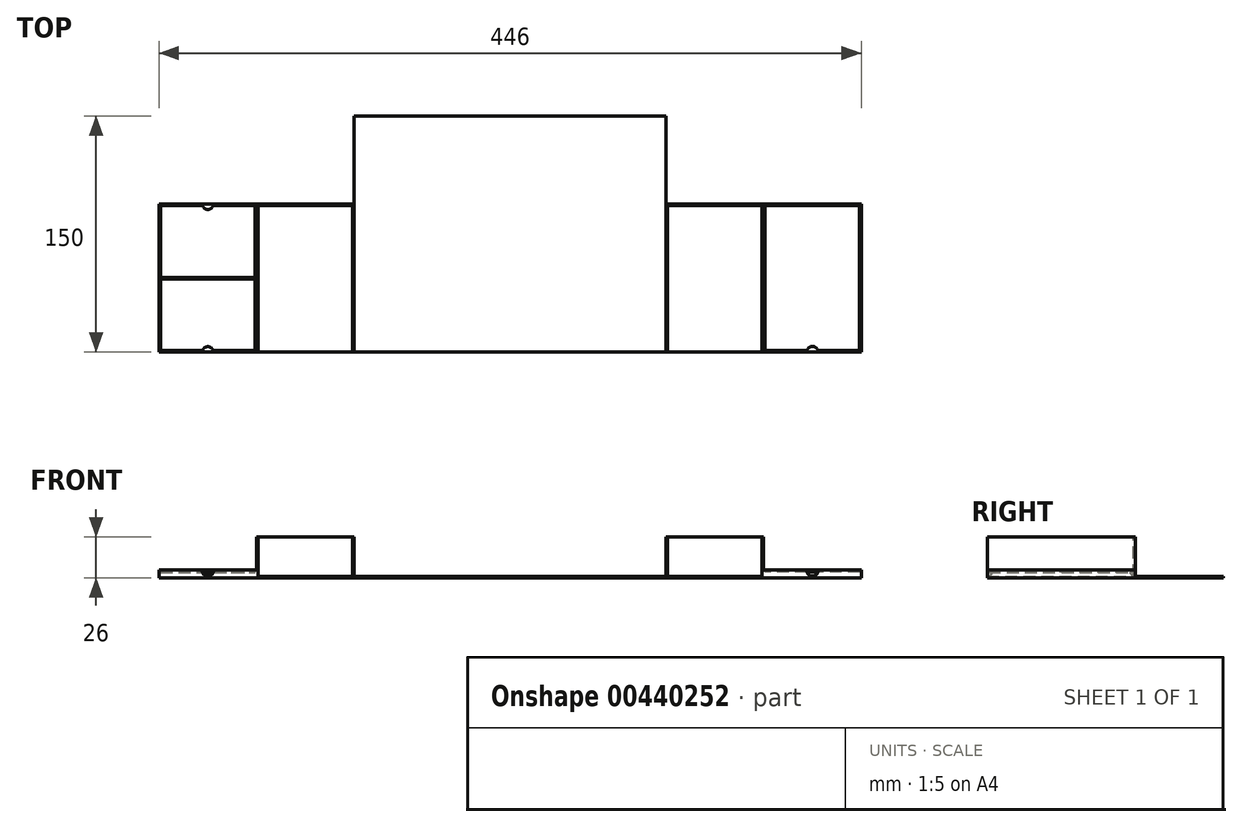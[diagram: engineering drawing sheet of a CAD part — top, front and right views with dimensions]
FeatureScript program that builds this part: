
annotation { "Feature Type Name" : "Feature", "Feature Type Description" : "" }
export const myFeature = defineFeature(function(context is Context, id is Id, definition is map)
    precondition{}
    {
        {
            var Q0;
            Q0=qCreatedBy(makeId("Top.planeOp"),FACE);
            var sketch = newSketch(context, id + "F0", { "sketchPlane" : qUnion([Q0])});
            skLineSegment(sketch, "E0", {"start": v(0, 0) * mm, "end": v(322, 0) * mm});
            skLineSegment(sketch, "E1", {"start": v(322, 0) * mm, "end": v(322, 94) * mm});
            skLineSegment(sketch, "E2", {"start": v(322, 94) * mm, "end": v(261, 94) * mm});
            skLineSegment(sketch, "E3", {"start": v(261, 94) * mm, "end": v(261, 150) * mm});
            skLineSegment(sketch, "E4", {"start": v(261, 150) * mm, "end": v(61, 150) * mm});
            skLineSegment(sketch, "E5", {"start": v(61, 150) * mm, "end": v(61, 94) * mm});
            skLineSegment(sketch, "E6", {"start": v(61, 94) * mm, "end": v(0, 94) * mm});
            skLineSegment(sketch, "E7", {"start": v(0, 94) * mm, "end": v(0, 0) * mm});
            skSolve(sketch);
        }
        {
            var Q0;
            Q0=makeQuery(id+"F0.imprint","IMPRINT",FACE,{"disambiguationData":[TD([[makeQuery(id+"F0.imprint","IMPRINT",EDGE,{"derivedFrom":sQuery(id+"F0.wireOp",EDGE,"E0")}),1.0]])]});
            extrude(context, id + "F1", {"entities" : qUnion([Q0]), "depth" : 26 * mm});
        }
        {
            var Q0;
            Q0=makeQuery(id+"F1.opExtrude","SWEPT_FACE",FACE,{"disambiguationData":[OSD([sQuery(id+"F0.wireOp",EDGE,"E7")])]});
            var sketch = newSketch(context, id + "F2", { "sketchPlane" : qUnion([Q0])});
            skLineSegment(sketch, "E8.bottom", {"start": v(0, 0) * mm, "end": v(-94, 0) * mm});
            skLineSegment(sketch, "E8.top", {"start": v(0, 5) * mm, "end": v(-94, 5) * mm});
            skLineSegment(sketch, "E8.left", {"start": v(0, 0) * mm, "end": v(0, 5) * mm});
            skLineSegment(sketch, "E8.right", {"start": v(-94, 0) * mm, "end": v(-94, 5) * mm});
            skSolve(sketch);
        }
        {
            var Q0;
            Q0=makeQuery(id+"F2.imprint","IMPRINT",FACE,{"disambiguationData":[TD([[makeQuery(id+"F2.imprint","IMPRINT",EDGE,{"derivedFrom":sQuery(id+"F2.wireOp",EDGE,"E8.bottom")}),1.0]])]});
            extrude(context, id + "F3", {"entities" : qUnion([Q0]), "operationType" : NewBodyOperationType.ADD, "depth" : 62 * mm});
        }
        {
            var Q0;
            Q0=makeQuery(id+"F3.opExtrude","SWEPT_FACE",FACE,{"disambiguationData":[OSD([sQuery(id+"F2.wireOp",EDGE,"E8.top")])]});
            var sketch = newSketch(context, id + "F4", { "sketchPlane" : qUnion([Q0])});
            skLineSegment(sketch, "E9", {"start": v(-62, 0) * mm, "end": v(-61, 0) * mm});
            skLineSegment(sketch, "E10", {"start": v(-61, 0) * mm, "end": v(-61, 1) * mm});
            skLineSegment(sketch, "E11.bottom", {"start": v(-61, 1) * mm, "end": v(-1, 1) * mm});
            skLineSegment(sketch, "E11.top", {"start": v(-61, 93) * mm, "end": v(-1, 93) * mm});
            skLineSegment(sketch, "E11.left", {"start": v(-61, 1) * mm, "end": v(-61, 93) * mm});
            skLineSegment(sketch, "E11.right", {"start": v(-1, 1) * mm, "end": v(-1, 93) * mm});
            skLineSegment(sketch, "E12", {"start": v(-61, 47) * mm, "end": v(-61, 47.5) * mm});
            skLineSegment(sketch, "E13", {"start": v(-61, 47.5) * mm, "end": v(-1, 47.5) * mm});
            skLineSegment(sketch, "E14", {"start": v(-61, 47) * mm, "end": v(-61, 46.5) * mm});
            skLineSegment(sketch, "E15", {"start": v(-61, 46.5) * mm, "end": v(-1, 46.5) * mm});
            skSolve(sketch);
        }
        {
            var Q0;
            {var subQ0=sQuery(id+"F4.wireOp",EDGE,"E11.top");Q0=makeQuery(id+"F4.imprint","IMPRINT",FACE,{"disambiguationData":[TD([[makeQuery(id+"F4.imprint","IMPRINT",EDGE,{"derivedFrom":subQ0}),-1.0]])]});}
            var Q1;
            {var subQ0=sQuery(id+"F4.wireOp",EDGE,"E11.bottom");Q1=makeQuery(id+"F4.imprint","IMPRINT",FACE,{"disambiguationData":[TD([[makeQuery(id+"F4.imprint","IMPRINT",EDGE,{"derivedFrom":subQ0}),1.0]])]});}
            extrude(context, id + "F5", {"entities" : qUnion([Q0, Q1]), "operationType" : NewBodyOperationType.REMOVE, "oppositeDirection" : true, "depth" : 1.5 * mm});
        }
        {
            var Q0;
            Q0=makeQuery(id+"F1.opExtrude","CAP_FACE",FACE,{"disambiguationData":[OSD([sQuery(id+"F0.wireOp",EDGE,"E0"),sQuery(id+"F0.wireOp",EDGE,"E1"),sQuery(id+"F0.wireOp",EDGE,"E2"),sQuery(id+"F0.wireOp",EDGE,"E3"),sQuery(id+"F0.wireOp",EDGE,"E4"),sQuery(id+"F0.wireOp",EDGE,"E5"),sQuery(id+"F0.wireOp",EDGE,"E6"),sQuery(id+"F0.wireOp",EDGE,"E7")])],"isStart":false});
            var sketch = newSketch(context, id + "F6", { "sketchPlane" : qUnion([Q0])});
            skLineSegment(sketch, "E16", {"start": v(0, 0) * mm, "end": v(1, 0) * mm});
            skLineSegment(sketch, "E17.bottom", {"start": v(1, 0) * mm, "end": v(61, 0) * mm});
            skLineSegment(sketch, "E17.top", {"start": v(1, 93) * mm, "end": v(61, 93) * mm});
            skLineSegment(sketch, "E17.left", {"start": v(1, 0) * mm, "end": v(1, 93) * mm});
            skLineSegment(sketch, "E17.right", {"start": v(61, 0) * mm, "end": v(61, 93) * mm});
            skLineSegment(sketch, "E18", {"start": v(161, 0) * mm, "end": v(161, 60) * mm});
            skLineSegment(sketch, "E19.MirrorCS", {"start": v(261, 0) * mm, "end": v(261, 93) * mm});
            skLineSegment(sketch, "E20.MirrorCS", {"start": v(321, 93) * mm, "end": v(261, 93) * mm});
            skLineSegment(sketch, "E21.MirrorCS", {"start": v(321, 0) * mm, "end": v(321, 93) * mm});
            skLineSegment(sketch, "E22.MirrorCS", {"start": v(321, 0) * mm, "end": v(261, 0) * mm});
            skSolve(sketch);
        }
        {
            var Q0;
            Q0=makeQuery(id+"F6.imprint","IMPRINT",FACE,{"disambiguationData":[TD([[makeQuery(id+"F6.imprint","IMPRINT",EDGE,{"derivedFrom":sQuery(id+"F6.wireOp",EDGE,"E17.bottom")}),1.0]])]});
            var Q1;
            Q1=makeQuery(id+"F6.imprint","IMPRINT",FACE,{"disambiguationData":[TD([[makeQuery(id+"F6.imprint","IMPRINT",EDGE,{"derivedFrom":sQuery(id+"F6.wireOp",EDGE,"E19.MirrorCS")}),-1.0]])]});
            extrude(context, id + "F7", {"entities" : qUnion([Q0, Q1]), "operationType" : NewBodyOperationType.REMOVE, "oppositeDirection" : true, "depth" : 25 * mm});
        }
        {
            var Q0;
            Q0=makeQuery(id+"F3.opExtrude","SWEPT_FACE",FACE,{"disambiguationData":[OSD([sQuery(id+"F2.wireOp",EDGE,"E8.top")])]});
            var sketch = newSketch(context, id + "F8", { "sketchPlane" : qUnion([Q0])});
            skCircle(sketch, "E23", {"center": v(-31, 0) * mm, "radius": 3.75 * mm});
            skCircle(sketch, "E24", {"center": v(-31, 94) * mm, "radius": 3.75 * mm});
            skSolve(sketch);
        }
        {
            var Q0;
            {var subQ0=sQuery(id+"F8.wireOp",EDGE,"E23");var subQ1=makeQuery(id+"F3.opExtrude","SWEPT_EDGE",EDGE,{"disambiguationData":[OSD([sQuery(id+"F0.wireOp",EDGE,"E0"),sQuery(id+"F0.wireOp",EDGE,"E7"),sQuery(id+"F2.wireOp",EDGE,"E8.top"),sQuery(id+"F2.wireOp",EDGE,"E8.left")])]});var subQ2=makeQuery(id+"F8.imprint","INTERSECT",VERTEX,{"disambiguationData":[OD(0.0)],"derivedFrom":[subQ1,subQ0]});Q0=makeQuery(id+"F8.imprint","IMPRINT",FACE,{"disambiguationData":[TD([[makeQuery(id+"F8.imprint","IMPRINT",EDGE,{"disambiguationData":[TD([[subQ2,1.0]])],"derivedFrom":subQ0}),1.0]])]});}
            var Q1;
            Q1=makeQuery(id+"F3.opExtrude","SWEPT_EDGE",EDGE,{"disambiguationData":[OSD([sQuery(id+"F0.wireOp",EDGE,"E0"),sQuery(id+"F0.wireOp",EDGE,"E7"),sQuery(id+"F2.wireOp",EDGE,"E8.top"),sQuery(id+"F2.wireOp",EDGE,"E8.left")])]});
            revolve(context, id + "F9", {"operationType" : NewBodyOperationType.REMOVE, "entities" : qUnion([Q0]), "axis" : qUnion([Q1]), "revolveType" : RevolveType.FULL, "oppositeDirection" : true});
        }
        {
            var Q0;
            {var subQ0=sQuery(id+"F8.wireOp",EDGE,"E24");var subQ1=makeQuery(id+"F3.opExtrude","SWEPT_EDGE",EDGE,{"disambiguationData":[OSD([sQuery(id+"F0.wireOp",EDGE,"E6"),sQuery(id+"F0.wireOp",EDGE,"E7"),sQuery(id+"F2.wireOp",EDGE,"E8.top"),sQuery(id+"F2.wireOp",EDGE,"E8.right")])]});var subQ2=makeQuery(id+"F8.imprint","INTERSECT",VERTEX,{"disambiguationData":[OD(0.0)],"derivedFrom":[subQ1,subQ0]});Q0=makeQuery(id+"F8.imprint","IMPRINT",FACE,{"disambiguationData":[TD([[makeQuery(id+"F8.imprint","IMPRINT",EDGE,{"disambiguationData":[TD([[subQ2,1.0]])],"derivedFrom":subQ0}),1.0]])]});}
            var Q1;
            Q1=makeQuery(id+"F3.opExtrude","SWEPT_EDGE",EDGE,{"disambiguationData":[OSD([sQuery(id+"F0.wireOp",EDGE,"E6"),sQuery(id+"F0.wireOp",EDGE,"E7"),sQuery(id+"F2.wireOp",EDGE,"E8.top"),sQuery(id+"F2.wireOp",EDGE,"E8.right")])]});
            revolve(context, id + "F10", {"operationType" : NewBodyOperationType.REMOVE, "entities" : qUnion([Q0]), "axis" : qUnion([Q1]), "revolveType" : RevolveType.FULL, "oppositeDirection" : true});
        }
        {
            var Q0;
            Q0=makeQuery(id+"F1.opExtrude","SWEPT_FACE",FACE,{"disambiguationData":[OSD([sQuery(id+"F0.wireOp",EDGE,"E1")])]});
            var sketch = newSketch(context, id + "F11", { "sketchPlane" : qUnion([Q0])});
            skLineSegment(sketch, "E25.bottom", {"start": v(0, 0) * mm, "end": v(94, 0) * mm});
            skLineSegment(sketch, "E25.top", {"start": v(0, 5) * mm, "end": v(94, 5) * mm});
            skLineSegment(sketch, "E25.left", {"start": v(0, 0) * mm, "end": v(0, 5) * mm});
            skLineSegment(sketch, "E25.right", {"start": v(94, 0) * mm, "end": v(94, 5) * mm});
            skSolve(sketch);
        }
        {
            var Q0;
            Q0=makeQuery(id+"F11.imprint","IMPRINT",FACE,{"disambiguationData":[TD([[makeQuery(id+"F11.imprint","IMPRINT",EDGE,{"derivedFrom":sQuery(id+"F11.wireOp",EDGE,"E25.bottom")}),1.0]])]});
            extrude(context, id + "F12", {"entities" : qUnion([Q0]), "operationType" : NewBodyOperationType.ADD, "depth" : 62 * mm});
        }
        {
            var Q0;
            Q0=makeQuery(id+"F12.opExtrude","SWEPT_FACE",FACE,{"disambiguationData":[OSD([sQuery(id+"F11.wireOp",EDGE,"E25.top")])]});
            var sketch = newSketch(context, id + "F13", { "sketchPlane" : qUnion([Q0])});
            skLineSegment(sketch, "E26", {"start": v(384, 0) * mm, "end": v(383, 0) * mm});
            skLineSegment(sketch, "E27", {"start": v(383, 0) * mm, "end": v(383, 1) * mm});
            skLineSegment(sketch, "E28.bottom", {"start": v(383, 1) * mm, "end": v(323, 1) * mm});
            skLineSegment(sketch, "E28.top", {"start": v(383, 93) * mm, "end": v(323, 93) * mm});
            skLineSegment(sketch, "E28.left", {"start": v(383, 1) * mm, "end": v(383, 93) * mm});
            skLineSegment(sketch, "E28.right", {"start": v(323, 1) * mm, "end": v(323, 93) * mm});
            skSolve(sketch);
        }
        {
            var Q0;
            Q0=makeQuery(id+"F13.imprint","IMPRINT",FACE,{"disambiguationData":[TD([[makeQuery(id+"F13.imprint","IMPRINT",EDGE,{"derivedFrom":sQuery(id+"F13.wireOp",EDGE,"E28.bottom")}),-1.0]])]});
            extrude(context, id + "F14", {"entities" : qUnion([Q0]), "operationType" : NewBodyOperationType.REMOVE, "oppositeDirection" : true, "depth" : 1 * mm});
        }
        {
            var Q0;
            Q0=makeQuery(id+"F12.opExtrude","SWEPT_FACE",FACE,{"disambiguationData":[OSD([sQuery(id+"F11.wireOp",EDGE,"E25.top")])]});
            var sketch = newSketch(context, id + "F15", { "sketchPlane" : qUnion([Q0])});
            skCircle(sketch, "E29", {"center": v(353, 0) * mm, "radius": 3.75 * mm});
            skSolve(sketch);
        }
        {
            var Q0;
            {var subQ0=sQuery(id+"F15.wireOp",EDGE,"E29");var subQ1=makeQuery(id+"F12.opExtrude","SWEPT_EDGE",EDGE,{"disambiguationData":[OSD([sQuery(id+"F0.wireOp",EDGE,"E0"),sQuery(id+"F0.wireOp",EDGE,"E1"),sQuery(id+"F11.wireOp",EDGE,"E25.top"),sQuery(id+"F11.wireOp",EDGE,"E25.left")])]});var subQ2=makeQuery(id+"F15.imprint","INTERSECT",VERTEX,{"disambiguationData":[OD(0.0)],"derivedFrom":[subQ1,subQ0]});Q0=makeQuery(id+"F15.imprint","IMPRINT",FACE,{"disambiguationData":[TD([[makeQuery(id+"F15.imprint","IMPRINT",EDGE,{"disambiguationData":[TD([[subQ2,1.0]])],"derivedFrom":subQ0}),1.0]])]});}
            var Q1;
            Q1=makeQuery(id+"F12.opExtrude","SWEPT_EDGE",EDGE,{"disambiguationData":[OSD([sQuery(id+"F0.wireOp",EDGE,"E0"),sQuery(id+"F0.wireOp",EDGE,"E1"),sQuery(id+"F11.wireOp",EDGE,"E25.top"),sQuery(id+"F11.wireOp",EDGE,"E25.left")])]});
            revolve(context, id + "F16", {"operationType" : NewBodyOperationType.REMOVE, "entities" : qUnion([Q0]), "axis" : qUnion([Q1]), "revolveType" : RevolveType.FULL, "oppositeDirection" : true});
        }
        {
            var Q0;
            Q0=makeQuery(id+"F1.opExtrude","CAP_FACE",FACE,{"disambiguationData":[OSD([sQuery(id+"F0.wireOp",EDGE,"E0"),sQuery(id+"F0.wireOp",EDGE,"E1"),sQuery(id+"F0.wireOp",EDGE,"E2"),sQuery(id+"F0.wireOp",EDGE,"E3"),sQuery(id+"F0.wireOp",EDGE,"E4"),sQuery(id+"F0.wireOp",EDGE,"E5"),sQuery(id+"F0.wireOp",EDGE,"E6"),sQuery(id+"F0.wireOp",EDGE,"E7")])],"isStart":false});
            var sketch = newSketch(context, id + "F17", { "sketchPlane" : qUnion([Q0])});
            skLineSegment(sketch, "E30", {"start": v(61, 0) * mm, "end": v(62, 0) * mm});
            skLineSegment(sketch, "E31.bottom", {"start": v(62, 0) * mm, "end": v(260, 0) * mm});
            skLineSegment(sketch, "E31.top", {"start": v(62, 150) * mm, "end": v(260, 150) * mm});
            skLineSegment(sketch, "E31.left", {"start": v(62, 0) * mm, "end": v(62, 150) * mm});
            skLineSegment(sketch, "E31.right", {"start": v(260, 0) * mm, "end": v(260, 150) * mm});
            skSolve(sketch);
        }
        {
            var Q0;
            Q0=makeQuery(id+"F17.imprint","IMPRINT",FACE,{"disambiguationData":[TD([[makeQuery(id+"F17.imprint","IMPRINT",EDGE,{"derivedFrom":sQuery(id+"F17.wireOp",EDGE,"E31.bottom")}),1.0]])]});
            extrude(context, id + "F18", {"entities" : qUnion([Q0]), "operationType" : NewBodyOperationType.REMOVE, "oppositeDirection" : true, "depth" : 25 * mm});
        }
        {
            var Q0;
            {var subQ0=sQuery(id+"F0.wireOp",EDGE,"E6");var subQ1=sQuery(id+"F0.wireOp",EDGE,"E7");var subQ2=sQuery(id+"F0.wireOp",EDGE,"E0");var subQ3=sQuery(id+"F0.wireOp",EDGE,"E4");var subQ4=sQuery(id+"F0.wireOp",EDGE,"E5");Q0=makeQuery(id+"F18.boolean.opBoolean","SPLIT",FACE,{"disambiguationData":[TD([makeQuery(id+"F1.opExtrude","SWEPT_FACE",FACE,{"disambiguationData":[OSD([subQ4])]})])],"derivedFrom":makeQuery(id+"F1.opExtrude","CAP_FACE",FACE,{"disambiguationData":[OSD([subQ2,sQuery(id+"F0.wireOp",EDGE,"E1"),sQuery(id+"F0.wireOp",EDGE,"E2"),sQuery(id+"F0.wireOp",EDGE,"E3"),subQ3,subQ4,subQ0,subQ1])],"isStart":false})});}
            var sketch = newSketch(context, id + "F19", { "sketchPlane" : qUnion([Q0])});
            skLineSegment(sketch, "E32.bottom", {"start": v(61, 94) * mm, "end": v(62, 94) * mm});
            skLineSegment(sketch, "E32.top", {"start": v(61, 150) * mm, "end": v(62, 150) * mm});
            skLineSegment(sketch, "E32.left", {"start": v(61, 94) * mm, "end": v(61, 150) * mm});
            skLineSegment(sketch, "E32.right", {"start": v(62, 94) * mm, "end": v(62, 150) * mm});
            skLineSegment(sketch, "E33", {"start": v(62, 94) * mm, "end": v(260, 94) * mm});
            skLineSegment(sketch, "E34.bottom", {"start": v(260, 94) * mm, "end": v(261, 94) * mm});
            skLineSegment(sketch, "E34.top", {"start": v(260, 150) * mm, "end": v(261, 150) * mm});
            skLineSegment(sketch, "E34.left", {"start": v(260, 94) * mm, "end": v(260, 150) * mm});
            skLineSegment(sketch, "E34.right", {"start": v(261, 94) * mm, "end": v(261, 150) * mm});
            skSolve(sketch);
        }
        {
            var Q0;
            Q0=makeQuery(id+"F19.imprint","IMPRINT",FACE,{"disambiguationData":[TD([[makeQuery(id+"F19.imprint","IMPRINT",EDGE,{"derivedFrom":sQuery(id+"F19.wireOp",EDGE,"E34.bottom")}),1.0]])]});
            var Q1;
            Q1=makeQuery(id+"F19.imprint","IMPRINT",FACE,{"disambiguationData":[TD([[makeQuery(id+"F19.imprint","IMPRINT",EDGE,{"derivedFrom":sQuery(id+"F19.wireOp",EDGE,"E32.bottom")}),1.0]])]});
            extrude(context, id + "F20", {"entities" : qUnion([Q0, Q1]), "operationType" : NewBodyOperationType.REMOVE, "oppositeDirection" : true, "depth" : 26 * mm});
        }
    });
